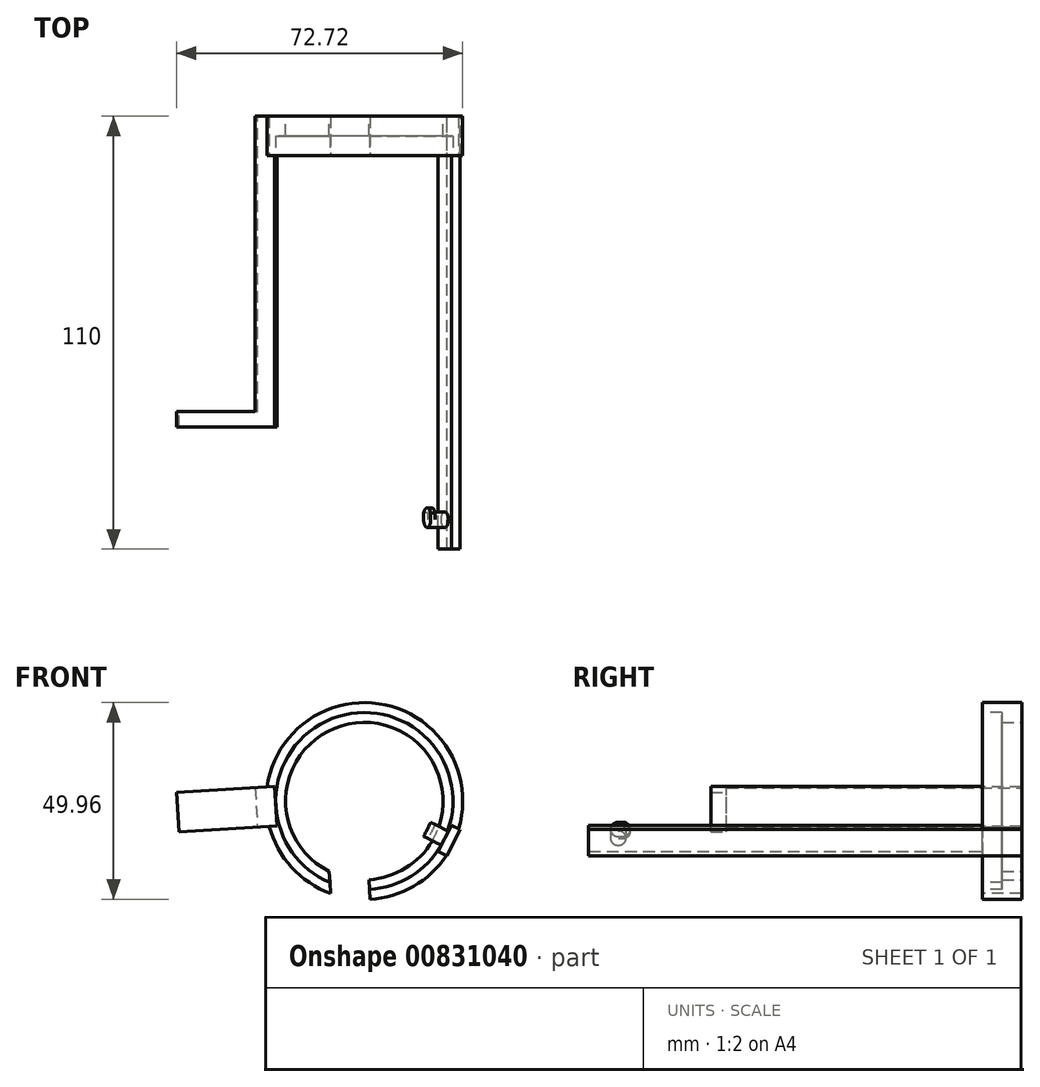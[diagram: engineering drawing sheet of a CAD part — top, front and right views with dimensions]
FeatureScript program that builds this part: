
annotation { "Feature Type Name" : "Feature", "Feature Type Description" : "" }
export const myFeature = defineFeature(function(context is Context, id is Id, definition is map)
    precondition{}
    {
        {
            var Q0;
            Q0=qCreatedBy(makeId("Front.planeOp"),FACE);
            var sketch = newSketch(context, id + "F0", { "sketchPlane" : qUnion([Q0])});
            skCircle(sketch, "E0", {"center": v(0, 0) * mm, "radius": 20 * mm});
            skCircle(sketch, "E1", {"center": v(0, 0) * mm, "radius": 23.5 * mm});
            skSolve(sketch);
        }
        {
            var Q0;
            Q0=makeQuery(id+"F0.imprint","IMPRINT",FACE,{"disambiguationData":[TD([[makeQuery(id+"F0.imprint","IMPRINT",EDGE,{"derivedFrom":sQuery(id+"F0.wireOp",EDGE,"E0")}),-1.0]])]});
            extrude(context, id + "F1", {"entities" : qUnion([Q0]), "offsetDistance" : 25 * mm, "depth" : 5 * mm});
        }
        {
            var Q0;
            Q0=qCreatedBy(makeId("Front.planeOp"),FACE);
            cPlane(context, id + "F2", {"entities" : qUnion([Q0]), "cplaneType" : CPlaneType.OFFSET, "offset" : 10 * mm, "width" : 150 * mm, "height" : 150 * mm});
        }
        {
            var Q0;
            Q0=qCreatedBy(id+"F2.planeOp",FACE);
            var sketch = newSketch(context, id + "F3", { "sketchPlane" : qUnion([Q0])});
            skCircle(sketch, "E2", {"center": v(0, 0) * mm, "radius": 22.5 * mm});
            skCircle(sketch, "E3", {"center": v(0, 0) * mm, "radius": 25 * mm});
            skSolve(sketch);
        }
        {
            var Q0;
            Q0=makeQuery(id+"F3.imprint","IMPRINT",FACE,{"disambiguationData":[TD([[makeQuery(id+"F3.imprint","IMPRINT",EDGE,{"derivedFrom":sQuery(id+"F3.wireOp",EDGE,"E2")}),-1.0]])]});
            extrude(context, id + "F4", {"entities" : qUnion([Q0]), "oppositeDirection" : true, "depth" : 10 * mm});
        }
        {
            var Q0;
            Q0=qCreatedBy(makeId("Front.planeOp"),FACE);
            var sketch = newSketch(context, id + "F5", { "sketchPlane" : qUnion([Q0])});
            skLineSegment(sketch, "E4", {"start": v(27.66, -0.58) * mm, "end": v(17.66, -0.58) * mm});
            skLineSegment(sketch, "E5.bottom", {"start": v(24.33, -7.24) * mm, "end": v(22.1, -6.12) * mm});
            skLineSegment(sketch, "E5.top", {"start": v(21, -13.9) * mm, "end": v(18.76, -12.8) * mm});
            skLineSegment(sketch, "E5.left", {"start": v(24.33, -7.24) * mm, "end": v(21, -13.9) * mm});
            skLineSegment(sketch, "E5.right", {"start": v(22.1, -6.12) * mm, "end": v(18.76, -12.8) * mm});
            skLineSegment(sketch, "E6", {"start": v(17.66, -0.58) * mm, "end": v(17.66, -20.58) * mm});
            skLineSegment(sketch, "E7", {"start": v(17.66, -20.58) * mm, "end": v(27.66, -20.58) * mm});
            skLineSegment(sketch, "E8", {"start": v(27.66, -20.58) * mm, "end": v(27.66, -0.58) * mm});
            skSolve(sketch);
        }
        {
            var Q0;
            Q0=makeQuery(id+"F5.imprint","IMPRINT",FACE,{"disambiguationData":[TD([[makeQuery(id+"F5.imprint","IMPRINT",EDGE,{"derivedFrom":sQuery(id+"F5.wireOp",EDGE,"E5.bottom")}),1.0]])]});
            extrude(context, id + "F6", {"entities" : qUnion([Q0]), "operationType" : NewBodyOperationType.ADD, "offsetDistance" : 25 * mm, "depth" : 110 * mm});
        }
        {
            var Q0;
            Q0=makeQuery(id+"F6.opExtrude","SWEPT_FACE",FACE,{"disambiguationData":[OSD([sQuery(id+"F5.wireOp",EDGE,"E5.left")])]});
            cPlane(context, id + "F7", {"entities" : qUnion([Q0]), "cplaneType" : CPlaneType.OFFSET, "offset" : 2.5 * mm, "oppositeDirection" : true, "width" : 150 * mm, "height" : 150 * mm});
        }
        {
            var Q0;
            Q0=qCreatedBy(id+"F7.planeOp",FACE);
            var sketch = newSketch(context, id + "F8", { "sketchPlane" : qUnion([Q0])});
            skLineSegment(sketch, "E9.bottom", {"start": v(-10, 4.41) * mm, "end": v(0, 4.41) * mm});
            skLineSegment(sketch, "E9.top", {"start": v(-10, -3.04) * mm, "end": v(0, -3.04) * mm});
            skLineSegment(sketch, "E9.left", {"start": v(-10, 4.41) * mm, "end": v(-10, -3.04) * mm});
            skLineSegment(sketch, "E9.right", {"start": v(0, 4.41) * mm, "end": v(0, -3.04) * mm});
            skSolve(sketch);
        }
        {
            var Q0;
            Q0=makeQuery(id+"F8.imprint","IMPRINT",FACE,{"disambiguationData":[TD([[makeQuery(id+"F8.imprint","IMPRINT",EDGE,{"derivedFrom":sQuery(id+"F8.wireOp",EDGE,"E9.bottom")}),-1.0]])]});
            extrude(context, id + "F9", {"entities" : qUnion([Q0]), "oppositeDirection" : true, "depth" : 2.5 * mm});
        }
        {
            var Q0;
            Q0=qCreatedBy(id+"F7.planeOp",FACE);
            var sketch = newSketch(context, id + "F10", { "sketchPlane" : qUnion([Q0])});
            skCircle(sketch, "E10", {"center": v(-102.5, 0.7) * mm, "radius": 2 * mm});
            skSolve(sketch);
        }
        {
            var Q0;
            Q0=qCreatedBy(makeId("Front.planeOp"),FACE);
            var sketch = newSketch(context, id + "F11", { "sketchPlane" : qUnion([Q0])});
            skLineSegment(sketch, "E11.bottom", {"start": v(-27.75, 3.4) * mm, "end": v(-27.15, -6.58) * mm});
            skLineSegment(sketch, "E11.top", {"start": v(-22.76, 3.7) * mm, "end": v(-22.16, -6.28) * mm});
            skLineSegment(sketch, "E11.left", {"start": v(-27.75, 3.4) * mm, "end": v(-22.76, 3.7) * mm});
            skLineSegment(sketch, "E11.right", {"start": v(-27.15, -6.58) * mm, "end": v(-22.16, -6.28) * mm});
            skSolve(sketch);
        }
        {
            var Q0;
            Q0=makeQuery(id+"F11.imprint","IMPRINT",FACE,{"disambiguationData":[TD([[makeQuery(id+"F11.imprint","IMPRINT",EDGE,{"derivedFrom":sQuery(id+"F11.wireOp",EDGE,"E11.bottom")}),1.0]])]});
            extrude(context, id + "F12", {"entities" : qUnion([Q0]), "operationType" : NewBodyOperationType.ADD, "offsetDistance" : 25 * mm, "depth" : 75 * mm});
        }
        {
            var Q0;
            Q0=makeQuery(id+"F9.opExtrude","SWEPT_BODY",BODY,{"disambiguationData":[OSD([sQuery(id+"F8.wireOp",EDGE,"E9.bottom"),sQuery(id+"F8.wireOp",EDGE,"E9.top"),sQuery(id+"F8.wireOp",EDGE,"E9.left"),sQuery(id+"F8.wireOp",EDGE,"E9.right")])]});
            deleteBodies(context, id + "F13", {"entities" : qUnion([Q0])});
        }
        {
            var Q0;
            Q0=makeQuery(id+"F10.imprint","IMPRINT",FACE,{"disambiguationData":[TD([[makeQuery(id+"F10.imprint","IMPRINT",EDGE,{"derivedFrom":sQuery(id+"F10.wireOp",EDGE,"E10")}),1.0]])]});
            extrude(context, id + "F14", {"entities" : qUnion([Q0]), "operationType" : NewBodyOperationType.ADD, "oppositeDirection" : true, "depth" : 5 * mm});
        }
        {
            var Q0;
            Q0=makeQuery(id+"F12.opExtrude","CAP_FACE",FACE,{"disambiguationData":[OSD([sQuery(id+"F11.wireOp",EDGE,"E11.bottom"),sQuery(id+"F11.wireOp",EDGE,"E11.top"),sQuery(id+"F11.wireOp",EDGE,"E11.left"),sQuery(id+"F11.wireOp",EDGE,"E11.right")])],"isStart":false});
            var sketch = newSketch(context, id + "F15", { "sketchPlane" : qUnion([Q0])});
            skLineSegment(sketch, "E12", {"start": v(-27.15, -6.58) * mm, "end": v(-22.16, -6.28) * mm});
            skLineSegment(sketch, "E13", {"start": v(-22.16, -6.28) * mm, "end": v(-22.76, 3.7) * mm});
            skLineSegment(sketch, "E14", {"start": v(-22.76, 3.7) * mm, "end": v(-27.75, 3.4) * mm});
            skLineSegment(sketch, "E15", {"start": v(-27.75, 3.4) * mm, "end": v(-27.15, -6.58) * mm});
            skSolve(sketch);
        }
        {
            var Q0;
            Q0=makeQuery(id+"F15.imprint","IMPRINT",FACE,{"disambiguationData":[TD([[makeQuery(id+"F15.imprint","IMPRINT",EDGE,{"derivedFrom":sQuery(id+"F15.wireOp",EDGE,"E12")}),1.0]])]});
            extrude(context, id + "F16", {"entities" : qUnion([Q0]), "operationType" : NewBodyOperationType.ADD, "depth" : 4 * mm});
        }
        {
            var Q0;
            Q0=makeQuery(id+"F14.opExtrude","CAP_FACE",FACE,{"disambiguationData":[OSD([sQuery(id+"F10.wireOp",EDGE,"E10")])],"isStart":false});
            var sketch = newSketch(context, id + "F17", { "sketchPlane" : qUnion([Q0])});
            skCircle(sketch, "E16", {"center": v(102.5, 0.7) * mm, "radius": 2 * mm});
            skPoint(sketch, "E16.first.point", {"position": v(100.5, 0.58) * mm});
            skPoint(sketch, "E16.second.point", {"position": v(104.5, 0.81) * mm});
            skPoint(sketch, "E16.third.point", {"position": v(100.5, 0.58) * mm});
            skLineSegment(sketch, "E17.bottom", {"start": v(104.5, -1.3) * mm, "end": v(99.5, -1.3) * mm});
            skLineSegment(sketch, "E17.top", {"start": v(104.5, 2.7) * mm, "end": v(99.5, 2.7) * mm});
            skLineSegment(sketch, "E17.left", {"start": v(104.5, -1.3) * mm, "end": v(104.5, 2.7) * mm});
            skLineSegment(sketch, "E17.right", {"start": v(99.5, -1.3) * mm, "end": v(99.5, 2.7) * mm});
            skSolve(sketch);
        }
        {
            var Q0;
            Q0=makeQuery(id+"F16.boolean.opBoolean","MERGE",FACE,{"derivedFrom":[makeQuery(id+"F12.opExtrude","SWEPT_FACE",FACE,{"disambiguationData":[OSD([sQuery(id+"F11.wireOp",EDGE,"E11.bottom")])]}),makeQuery(id+"F16.opExtrude","SWEPT_FACE",FACE,{"disambiguationData":[OSD([sQuery(id+"F15.wireOp",EDGE,"E15")])]})]});
            var sketch = newSketch(context, id + "F18", { "sketchPlane" : qUnion([Q0])});
            skLineSegment(sketch, "E18", {"start": v(79, 5.06) * mm, "end": v(79, -4.94) * mm});
            skLineSegment(sketch, "E19", {"start": v(79, -4.94) * mm, "end": v(75, -4.94) * mm});
            skLineSegment(sketch, "E20", {"start": v(75, -4.94) * mm, "end": v(75, 5.06) * mm});
            skLineSegment(sketch, "E21", {"start": v(75, 5.06) * mm, "end": v(79, 5.06) * mm});
            skSolve(sketch);
        }
        {
            var Q0;
            Q0=makeQuery(id+"F18.imprint","IMPRINT",FACE,{"disambiguationData":[TD([[makeQuery(id+"F18.imprint","IMPRINT",EDGE,{"derivedFrom":sQuery(id+"F18.wireOp",EDGE,"E18")}),-1.0]])]});
            extrude(context, id + "F19", {"entities" : qUnion([Q0]), "operationType" : NewBodyOperationType.ADD, "depth" : 20 * mm});
        }
        {
            var Q0;
            Q0=makeQuery(id+"F19.boolean.opBoolean","MERGE",FACE,{"derivedFrom":[makeQuery(id+"F16.boolean.opBoolean","MERGE",FACE,{"derivedFrom":[makeQuery(id+"F12.opExtrude","SWEPT_FACE",FACE,{"disambiguationData":[OSD([sQuery(id+"F11.wireOp",EDGE,"E11.right")])]}),makeQuery(id+"F16.opExtrude","SWEPT_FACE",FACE,{"disambiguationData":[OSD([sQuery(id+"F15.wireOp",EDGE,"E12")])]})]}),makeQuery(id+"F19.opExtrude","SWEPT_FACE",FACE,{"disambiguationData":[OSD([sQuery(id+"F18.wireOp",EDGE,"E19")])]})]});
            var sketch = newSketch(context, id + "F20", { "sketchPlane" : qUnion([Q0])});
            skLineSegment(sketch, "E22.bottom", {"start": v(-10, 0) * mm, "end": v(0, 0) * mm});
            skLineSegment(sketch, "E22.top", {"start": v(-10, 21.78) * mm, "end": v(0, 21.78) * mm});
            skLineSegment(sketch, "E22.left", {"start": v(0, 0) * mm, "end": v(0, 21.78) * mm});
            skLineSegment(sketch, "E22.right", {"start": v(-10, 0) * mm, "end": v(-10, 21.78) * mm});
            skSolve(sketch);
        }
        {
            var Q0;
            Q0=makeQuery(id+"F20.imprint","IMPRINT",FACE,{"disambiguationData":[TD([[makeQuery(id+"F20.imprint","IMPRINT",EDGE,{"derivedFrom":sQuery(id+"F20.wireOp",EDGE,"E22.bottom")}),1.0]])]});
            extrude(context, id + "F21", {"entities" : qUnion([Q0]), "operationType" : NewBodyOperationType.REMOVE, "depth" : 112 * mm, "offsetDistance" : 25 * mm});
        }
        {
            var Q0;
            {var subQ5=sQuery(id+"F17.wireOp",EDGE,"E17.right");Q0=makeQuery(id+"F17.imprint","IMPRINT",FACE,{"disambiguationData":[TD([[makeQuery(id+"F17.imprint","IMPRINT",EDGE,{"derivedFrom":subQ5}),-1.0]])]});}
            extrude(context, id + "F22", {"entities" : qUnion([Q0]), "operationType" : NewBodyOperationType.ADD, "oppositeDirection" : true, "depth" : 1.25 * mm, "offsetDistance" : 25 * mm});
        }
        {
            var Q0;
            Q0=makeQuery(id+"F22.boolean.opBoolean","MERGE",FACE,{"derivedFrom":[makeQuery(id+"F14.opExtrude","CAP_FACE",FACE,{"disambiguationData":[OSD([sQuery(id+"F10.wireOp",EDGE,"E10")])],"isStart":false}),makeQuery(id+"F22.opExtrude","CAP_FACE",FACE,{"disambiguationData":[OSD([sQuery(id+"F17.wireOp",EDGE,"E16"),sQuery(id+"F17.wireOp",EDGE,"E17.bottom"),sQuery(id+"F17.wireOp",EDGE,"E17.top"),sQuery(id+"F17.wireOp",EDGE,"E17.right")])],"isStart":true})]});
            var sketch = newSketch(context, id + "F23", { "sketchPlane" : qUnion([Q0])});
            skArc(sketch, "E23.0.0", {"start": v(102.5, -1.3) * mm, "mid": v(104.5, 0.7) * mm, "end": v(102.5, 2.7) * mm});
            skLineSegment(sketch, "E23.0.1", {"start": v(102.5, 2.7) * mm, "end": v(99.5, 2.7) * mm});
            skLineSegment(sketch, "E23.0.2", {"start": v(99.5, 2.7) * mm, "end": v(99.5, -1.3) * mm});
            skLineSegment(sketch, "E23.0.3", {"start": v(99.5, -1.3) * mm, "end": v(102.5, -1.3) * mm});
            skArc(sketch, "E24", {"start": v(102.5, 2.7) * mm, "mid": v(99.5, 0.7) * mm, "end": v(102.5, -1.3) * mm});
            skSolve(sketch);
        }
        {
            var Q0;
            {var subQ0=sQuery(id+"F23.wireOp",EDGE,"E23.0.3");var subQ1=sQuery(id+"F23.wireOp",EDGE,"E23.0.2");var subQ2=makeQuery(id+"F23.imprint","INTERSECT",VERTEX,{"derivedFrom":[subQ1,subQ0]});Q0=makeQuery(id+"F23.imprint","IMPRINT",FACE,{"disambiguationData":[TD([[makeQuery(id+"F23.imprint","IMPRINT",EDGE,{"disambiguationData":[TD([[subQ2,-1.0]])],"derivedFrom":subQ1}),-1.0]])]});}
            var Q1;
            {var subQ0=sQuery(id+"F23.wireOp",EDGE,"E23.0.2");var subQ1=sQuery(id+"F23.wireOp",EDGE,"E23.0.1");var subQ2=makeQuery(id+"F23.imprint","INTERSECT",VERTEX,{"derivedFrom":[subQ1,subQ0]});Q1=makeQuery(id+"F23.imprint","IMPRINT",FACE,{"disambiguationData":[TD([[makeQuery(id+"F23.imprint","IMPRINT",EDGE,{"disambiguationData":[TD([[subQ2,1.0]])],"derivedFrom":subQ1}),1.0]])]});}
            extrude(context, id + "F24", {"entities" : qUnion([Q0, Q1]), "operationType" : NewBodyOperationType.REMOVE, "oppositeDirection" : true, "depth" : 5 * mm, "offsetDistance" : 25 * mm});
        }
    });
